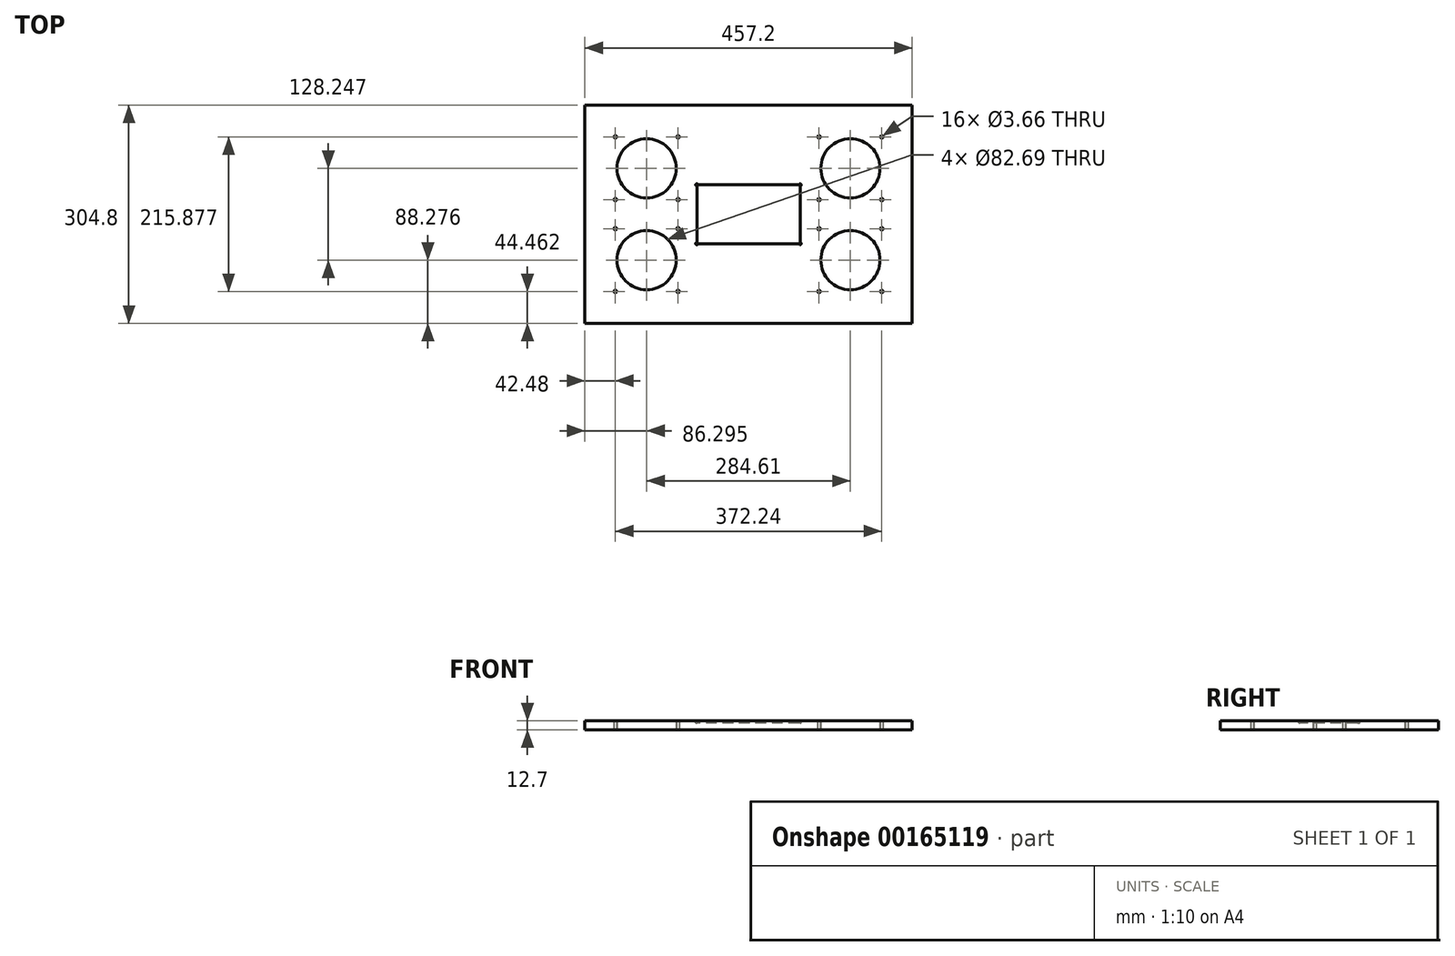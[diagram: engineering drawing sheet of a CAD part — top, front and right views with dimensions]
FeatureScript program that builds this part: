
annotation { "Feature Type Name" : "Feature", "Feature Type Description" : "" }
export const myFeature = defineFeature(function(context is Context, id is Id, definition is map)
    precondition{}
    {
        {
            var Q0;
            Q0=qCreatedBy(makeId("Top.planeOp"),FACE);
            var sketch = newSketch(context, id + "F0", { "sketchPlane" : qUnion([Q0])});
            skLineSegment(sketch, "E0.bottom", {"start": v(228.6, -152.4) * mm, "end": v(-228.6, -152.4) * mm});
            skLineSegment(sketch, "E0.top", {"start": v(228.6, 152.4) * mm, "end": v(-228.6, 152.4) * mm});
            skLineSegment(sketch, "E0.left", {"start": v(228.6, -152.4) * mm, "end": v(228.6, 152.4) * mm});
            skLineSegment(sketch, "E0.right", {"start": v(-228.6, -152.4) * mm, "end": v(-228.6, 152.4) * mm});
            skPoint(sketch, "E0.middle", {"position": v(0, 0) * mm});
            skLineSegment(sketch, "E1.bottom", {"start": v(142.3, -64.12) * mm, "end": v(-142.3, -64.12) * mm, "construction": true});
            skLineSegment(sketch, "E1.top", {"start": v(142.3, 64.12) * mm, "end": v(-142.3, 64.12) * mm, "construction": true});
            skLineSegment(sketch, "E1.left", {"start": v(142.3, -64.12) * mm, "end": v(142.3, 64.12) * mm, "construction": true});
            skLineSegment(sketch, "E1.right", {"start": v(-142.3, -64.12) * mm, "end": v(-142.3, 64.12) * mm, "construction": true});
            skLineSegment(sketch, "E2", {"start": v(142.3, -64.12) * mm, "end": v(142.3, -152.4) * mm, "construction": true});
            skLineSegment(sketch, "E3", {"start": v(142.3, -64.12) * mm, "end": v(228.6, -64.12) * mm, "construction": true});
            skLineSegment(sketch, "E4.bottom", {"start": v(186.12, -107.94) * mm, "end": v(98.5, -107.94) * mm, "construction": true});
            skLineSegment(sketch, "E4.top", {"start": v(186.12, -20.3) * mm, "end": v(98.5, -20.3) * mm, "construction": true});
            skLineSegment(sketch, "E4.left", {"start": v(186.12, -107.94) * mm, "end": v(186.12, -20.3) * mm, "construction": true});
            skLineSegment(sketch, "E4.right", {"start": v(98.5, -107.94) * mm, "end": v(98.5, -20.3) * mm, "construction": true});
            skPoint(sketch, "E4.middle", {"position": v(142.3, -64.12) * mm});
            skLineSegment(sketch, "E5.bottom", {"start": v(186.12, 20.3) * mm, "end": v(98.5, 20.3) * mm, "construction": true});
            skLineSegment(sketch, "E5.top", {"start": v(186.12, 107.94) * mm, "end": v(98.5, 107.94) * mm, "construction": true});
            skLineSegment(sketch, "E5.left", {"start": v(186.12, 20.3) * mm, "end": v(186.12, 107.94) * mm, "construction": true});
            skLineSegment(sketch, "E5.right", {"start": v(98.5, 20.3) * mm, "end": v(98.5, 107.94) * mm, "construction": true});
            skPoint(sketch, "E5.middle", {"position": v(142.3, 64.12) * mm});
            skLineSegment(sketch, "E6.bottom", {"start": v(-98.5, 107.94) * mm, "end": v(-186.12, 107.94) * mm, "construction": true});
            skLineSegment(sketch, "E6.top", {"start": v(-98.5, 20.3) * mm, "end": v(-186.12, 20.3) * mm, "construction": true});
            skLineSegment(sketch, "E6.left", {"start": v(-98.5, 107.94) * mm, "end": v(-98.5, 20.3) * mm, "construction": true});
            skLineSegment(sketch, "E6.right", {"start": v(-186.12, 107.94) * mm, "end": v(-186.12, 20.3) * mm, "construction": true});
            skPoint(sketch, "E6.middle", {"position": v(-142.3, 64.12) * mm});
            skLineSegment(sketch, "E7.bottom", {"start": v(-186.12, -107.94) * mm, "end": v(-98.5, -107.94) * mm, "construction": true});
            skLineSegment(sketch, "E7.top", {"start": v(-186.12, -20.3) * mm, "end": v(-98.5, -20.3) * mm, "construction": true});
            skLineSegment(sketch, "E7.left", {"start": v(-186.12, -107.94) * mm, "end": v(-186.12, -20.3) * mm, "construction": true});
            skLineSegment(sketch, "E7.right", {"start": v(-98.5, -107.94) * mm, "end": v(-98.5, -20.3) * mm, "construction": true});
            skPoint(sketch, "E7.middle", {"position": v(-142.3, -64.12) * mm});
            skCircle(sketch, "E8", {"center": v(142.3, 64.12) * mm, "radius": 41.34 * mm});
            skCircle(sketch, "E9", {"center": v(142.3, -64.12) * mm, "radius": 41.34 * mm});
            skCircle(sketch, "E10", {"center": v(-142.3, -64.12) * mm, "radius": 41.34 * mm});
            skCircle(sketch, "E11", {"center": v(-142.3, 64.12) * mm, "radius": 41.34 * mm});
            skCircle(sketch, "E12", {"center": v(98.5, -107.94) * mm, "radius": 1.83 * mm});
            skCircle(sketch, "E13", {"center": v(98.5, -20.3) * mm, "radius": 1.83 * mm});
            skCircle(sketch, "E14", {"center": v(186.12, -107.94) * mm, "radius": 1.83 * mm});
            skCircle(sketch, "E15", {"center": v(186.12, -20.3) * mm, "radius": 1.83 * mm});
            skCircle(sketch, "E16", {"center": v(186.12, 20.3) * mm, "radius": 1.83 * mm});
            skCircle(sketch, "E17", {"center": v(186.12, 107.94) * mm, "radius": 1.83 * mm});
            skCircle(sketch, "E18", {"center": v(98.5, 107.94) * mm, "radius": 1.83 * mm});
            skCircle(sketch, "E19", {"center": v(98.5, 20.3) * mm, "radius": 1.83 * mm});
            skCircle(sketch, "E20", {"center": v(-186.12, 20.3) * mm, "radius": 1.83 * mm});
            skCircle(sketch, "E21", {"center": v(-98.5, 20.3) * mm, "radius": 1.83 * mm});
            skCircle(sketch, "E22", {"center": v(-186.12, 107.94) * mm, "radius": 1.83 * mm});
            skCircle(sketch, "E23", {"center": v(-98.5, 107.94) * mm, "radius": 1.83 * mm});
            skCircle(sketch, "E24", {"center": v(-98.5, -107.94) * mm, "radius": 1.83 * mm});
            skCircle(sketch, "E25", {"center": v(-98.5, -20.3) * mm, "radius": 1.83 * mm});
            skCircle(sketch, "E26", {"center": v(-186.12, -20.3) * mm, "radius": 1.83 * mm});
            skCircle(sketch, "E27", {"center": v(-186.12, -107.94) * mm, "radius": 1.83 * mm});
            skSolve(sketch);
        }
        {
            var Q0;
            Q0 = qSketchRegion(id + "F0", true);
            extrude(context, id + "F1", {"entities" : qUnion([Q0]), "depth" : 12.7 * mm});
        }
        {
            var Q0;
            Q0=makeQuery(id+"F1.opExtrude","CAP_FACE",FACE,{"disambiguationData":[OSD([sQuery(id+"F0.wireOp",EDGE,"E0.bottom"),sQuery(id+"F0.wireOp",EDGE,"E0.top"),sQuery(id+"F0.wireOp",EDGE,"E0.left"),sQuery(id+"F0.wireOp",EDGE,"E0.right"),sQuery(id+"F0.wireOp",EDGE,"E8"),sQuery(id+"F0.wireOp",EDGE,"E9"),sQuery(id+"F0.wireOp",EDGE,"E10"),sQuery(id+"F0.wireOp",EDGE,"E11"),sQuery(id+"F0.wireOp",EDGE,"E12"),sQuery(id+"F0.wireOp",EDGE,"E13"),sQuery(id+"F0.wireOp",EDGE,"E14"),sQuery(id+"F0.wireOp",EDGE,"E15"),sQuery(id+"F0.wireOp",EDGE,"E16"),sQuery(id+"F0.wireOp",EDGE,"E17"),sQuery(id+"F0.wireOp",EDGE,"E18"),sQuery(id+"F0.wireOp",EDGE,"E19"),sQuery(id+"F0.wireOp",EDGE,"E20"),sQuery(id+"F0.wireOp",EDGE,"E21"),sQuery(id+"F0.wireOp",EDGE,"E22"),sQuery(id+"F0.wireOp",EDGE,"E23"),sQuery(id+"F0.wireOp",EDGE,"E24"),sQuery(id+"F0.wireOp",EDGE,"E25"),sQuery(id+"F0.wireOp",EDGE,"E26"),sQuery(id+"F0.wireOp",EDGE,"E27")])],"isStart":false});
            var sketch = newSketch(context, id + "F2", { "sketchPlane" : qUnion([Q0])});
            skLineSegment(sketch, "E28.bottom", {"start": v(72.2, 41.02) * mm, "end": v(-72.2, 41.02) * mm});
            skLineSegment(sketch, "E28.top", {"start": v(72.2, -41.02) * mm, "end": v(-72.2, -41.02) * mm});
            skLineSegment(sketch, "E28.left", {"start": v(72.2, 41.02) * mm, "end": v(72.2, -41.02) * mm});
            skLineSegment(sketch, "E28.right", {"start": v(-72.2, 41.02) * mm, "end": v(-72.2, -41.02) * mm});
            skPoint(sketch, "E28.middle", {"position": v(0, 0) * mm});
            skSolve(sketch);
        }
        {
            var Q0;
            Q0 = qSketchRegion(id + "F2", true);
            extrude(context, id + "F3", {"entities" : qUnion([Q0]), "operationType" : NewBodyOperationType.REMOVE, "oppositeDirection" : true, "depth" : 3.17 * mm});
        }
        {
            var Q0;
            Q0=makeQuery(id+"F1.opExtrude","CAP_FACE",FACE,{"disambiguationData":[OSD([sQuery(id+"F0.wireOp",EDGE,"E0.bottom"),sQuery(id+"F0.wireOp",EDGE,"E0.top"),sQuery(id+"F0.wireOp",EDGE,"E0.left"),sQuery(id+"F0.wireOp",EDGE,"E0.right"),sQuery(id+"F0.wireOp",EDGE,"E8"),sQuery(id+"F0.wireOp",EDGE,"E9"),sQuery(id+"F0.wireOp",EDGE,"E10"),sQuery(id+"F0.wireOp",EDGE,"E11"),sQuery(id+"F0.wireOp",EDGE,"E12"),sQuery(id+"F0.wireOp",EDGE,"E13"),sQuery(id+"F0.wireOp",EDGE,"E14"),sQuery(id+"F0.wireOp",EDGE,"E15"),sQuery(id+"F0.wireOp",EDGE,"E16"),sQuery(id+"F0.wireOp",EDGE,"E17"),sQuery(id+"F0.wireOp",EDGE,"E18"),sQuery(id+"F0.wireOp",EDGE,"E19"),sQuery(id+"F0.wireOp",EDGE,"E20"),sQuery(id+"F0.wireOp",EDGE,"E21"),sQuery(id+"F0.wireOp",EDGE,"E22"),sQuery(id+"F0.wireOp",EDGE,"E23"),sQuery(id+"F0.wireOp",EDGE,"E24"),sQuery(id+"F0.wireOp",EDGE,"E25"),sQuery(id+"F0.wireOp",EDGE,"E26"),sQuery(id+"F0.wireOp",EDGE,"E27")])],"isStart":false});
            var sketch = newSketch(context, id + "F4", { "sketchPlane" : qUnion([Q0])});
            skCircle(sketch, "E29", {"center": v(-72.2, 41.02) * mm, "radius": 1.59 * mm});
            skCircle(sketch, "E30", {"center": v(72.2, 41.02) * mm, "radius": 1.59 * mm});
            skCircle(sketch, "E31", {"center": v(72.2, -41.02) * mm, "radius": 1.59 * mm});
            skCircle(sketch, "E32", {"center": v(-72.2, -41.02) * mm, "radius": 1.59 * mm});
            skSolve(sketch);
        }
        {
            var Q0;
            Q0 = qSketchRegion(id + "F4", true);
            var Q1;
            Q1=makeQuery(id+"F3.boolean.opBoolean","COPY",FACE,{"derivedFrom":makeQuery(id+"F3.opExtrude","CAP_FACE",FACE,{"disambiguationData":[OSD([sQuery(id+"F2.wireOp",EDGE,"E28.bottom"),sQuery(id+"F2.wireOp",EDGE,"E28.top"),sQuery(id+"F2.wireOp",EDGE,"E28.left"),sQuery(id+"F2.wireOp",EDGE,"E28.right")])],"isStart":false})});
            extrude(context, id + "F5", {"entities" : qUnion([Q0]), "operationType" : NewBodyOperationType.REMOVE, "endBound" : BoundingType.UP_TO_SURFACE, "oppositeDirection" : true, "endBoundEntityFace" : qUnion([Q1]), "depth" : 25.4 * mm});
        }
    });
